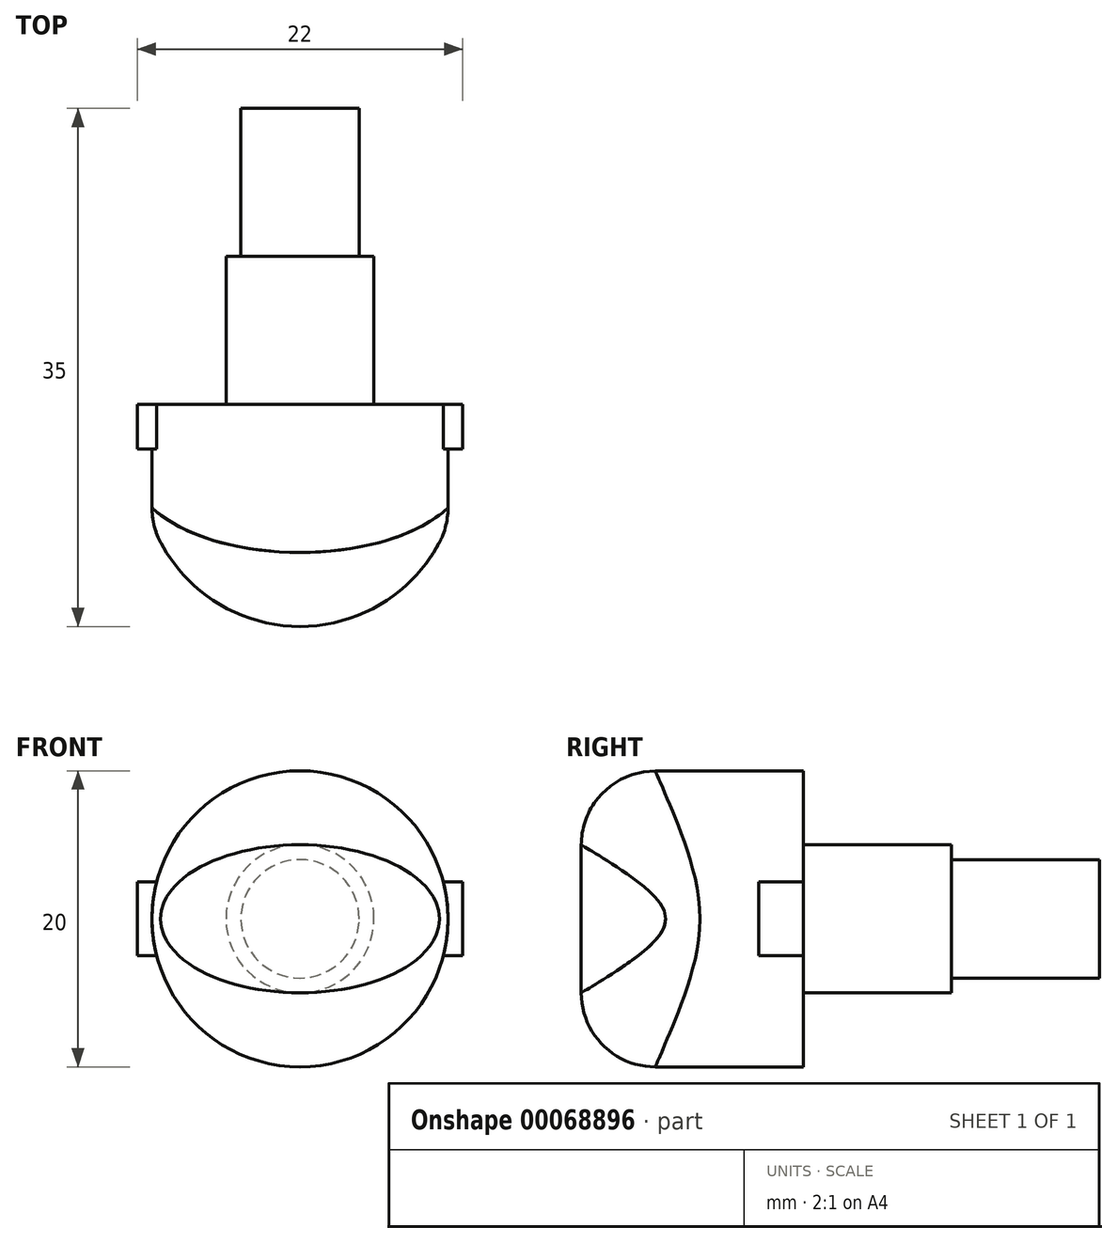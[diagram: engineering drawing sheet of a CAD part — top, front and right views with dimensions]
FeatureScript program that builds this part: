
annotation { "Feature Type Name" : "Feature", "Feature Type Description" : "" }
export const myFeature = defineFeature(function(context is Context, id is Id, definition is map)
    precondition{}
    {
        {
            var Q0;
            Q0=qCreatedBy(makeId("Front.planeOp"),FACE);
            var sketch = newSketch(context, id + "F0", { "sketchPlane" : qUnion([Q0])});
            skCircle(sketch, "E0", {"center": v(0, 0) * mm, "radius": 10 * mm});
            skLineSegment(sketch, "E1", {"start": v(11, 2.5) * mm, "end": v(11, -2.5) * mm});
            skLineSegment(sketch, "E2", {"start": v(11, -2.5) * mm, "end": v(9.68, -2.5) * mm});
            skLineSegment(sketch, "E3", {"start": v(11, 2.5) * mm, "end": v(9.68, 2.5) * mm});
            skLineSegment(sketch, "E4.MirrorCS", {"start": v(-11, -2.5) * mm, "end": v(-9.68, -2.5) * mm});
            skLineSegment(sketch, "E5.MirrorCS", {"start": v(-11, 2.5) * mm, "end": v(-9.68, 2.5) * mm});
            skLineSegment(sketch, "E6.MirrorCS", {"start": v(-11, 2.5) * mm, "end": v(-11, -2.5) * mm});
            skSolve(sketch);
        }
        {
            var Q0;
            Q0=qSketchRegion(id+"F0",true);
            var Q1;
            {var subQ0=sQuery(id+"F0.wireOp",EDGE,"E0");var subQ1=makeQuery(id+"F0.imprint","INTERSECT",VERTEX,{"derivedFrom":[subQ0,sQuery(id+"F0.wireOp",EDGE,"E3")]});Q1=makeQuery(id+"F0.imprint","IMPRINT",FACE,{"disambiguationData":[TD([[makeQuery(id+"F0.imprint","IMPRINT",EDGE,{"disambiguationData":[TD([[subQ1,-1.0]])],"derivedFrom":subQ0}),1.0]])]});}
            extrude(context, id + "F1", {"entities" : qUnion([Q0, Q1]), "oppositeDirection" : true, "depth" : 3 * mm});
        }
        {
            var Q0;
            Q0=qCreatedBy(makeId("Top.planeOp"),FACE);
            var sketch = newSketch(context, id + "F2", { "sketchPlane" : qUnion([Q0])});
            skLineSegment(sketch, "E7", {"start": v(0, 0) * mm, "end": v(-10, 0) * mm});
            skLineSegment(sketch, "E8", {"start": v(-10, 0) * mm, "end": v(-10, -5) * mm});
            skLineSegment(sketch, "E9", {"start": v(0, 0) * mm, "end": v(0, -12) * mm, "construction": true});
            skLineSegment(sketch, "E10", {"start": v(0, 0) * mm, "end": v(10, 0) * mm});
            skLineSegment(sketch, "E11", {"start": v(10, 0) * mm, "end": v(10, -5) * mm});
            skArc(sketch, "E12", {"start": v(-10, -5) * mm, "mid": v(0, -12) * mm, "end": v(10, -5) * mm});
            skSolve(sketch);
        }
        {
            var Q0;
            Q0=makeQuery(id+"F2.imprint","IMPRINT",FACE,{"disambiguationData":[TD([[makeQuery(id+"F2.imprint","IMPRINT",EDGE,{"derivedFrom":sQuery(id+"F2.wireOp",EDGE,"E7")}),1.0]])]});
            extrude(context, id + "F3", {"entities" : qUnion([Q0]), "operationType" : NewBodyOperationType.ADD, "endBound" : BoundingType.SYMMETRIC, "depth" : 20 * mm});
        }
        {
            var Q0;
            Q0=makeQuery(id+"F3.opExtrude","CAP_EDGE",EDGE,{"disambiguationData":[OSD([sQuery(id+"F2.wireOp",EDGE,"E11")])],"isStart":true});
            var Q1;
            Q1=makeQuery(id+"F3.opExtrude","CAP_EDGE",EDGE,{"disambiguationData":[OSD([sQuery(id+"F2.wireOp",EDGE,"E8")])],"isStart":true});
            var Q2;
            Q2=makeQuery(id+"F3.opExtrude","CAP_EDGE",EDGE,{"disambiguationData":[OSD([sQuery(id+"F2.wireOp",EDGE,"E11")])],"isStart":false});
            var Q3;
            Q3=makeQuery(id+"F3.opExtrude","CAP_EDGE",EDGE,{"disambiguationData":[OSD([sQuery(id+"F2.wireOp",EDGE,"E8")])],"isStart":false});
            fillet(context, id + "F4", {"entities" : qUnion([Q0, Q1, Q2, Q3]), "radius" : 10 * mm, "tangentPropagation" : true, "allowEdgeOverflow" : false});
        }
        {
            var Q0;
            Q0=makeQuery(id+"F4.opFillet","BLEND_EDGE",EDGE,{"blendedFrom":[makeQuery(id+"F3.opExtrude","CAP_EDGE",EDGE,{"disambiguationData":[OSD([sQuery(id+"F2.wireOp",EDGE,"E11")])],"isStart":false}),makeQuery(id+"F3.opExtrude","SWEPT_FACE",FACE,{"disambiguationData":[OSD([sQuery(id+"F2.wireOp",EDGE,"E12")])]})],"blendedInto":[makeQuery(id+"F3.opExtrude","SWEPT_FACE",FACE,{"disambiguationData":[OSD([sQuery(id+"F2.wireOp",EDGE,"E12")])]})]});
            var Q1;
            Q1=makeQuery(id+"F4.opFillet","BLEND_EDGE",EDGE,{"blendedFrom":[makeQuery(id+"F3.opExtrude","CAP_EDGE",EDGE,{"disambiguationData":[OSD([sQuery(id+"F2.wireOp",EDGE,"E8")])],"isStart":false}),makeQuery(id+"F3.opExtrude","SWEPT_FACE",FACE,{"disambiguationData":[OSD([sQuery(id+"F2.wireOp",EDGE,"E12")])]})],"blendedInto":[makeQuery(id+"F3.opExtrude","SWEPT_FACE",FACE,{"disambiguationData":[OSD([sQuery(id+"F2.wireOp",EDGE,"E12")])]})]});
            var Q2;
            Q2=makeQuery(id+"F4.opFillet","BLEND_EDGE",EDGE,{"blendedFrom":[makeQuery(id+"F3.opExtrude","CAP_EDGE",EDGE,{"disambiguationData":[OSD([sQuery(id+"F2.wireOp",EDGE,"E11")])],"isStart":true}),makeQuery(id+"F3.opExtrude","SWEPT_FACE",FACE,{"disambiguationData":[OSD([sQuery(id+"F2.wireOp",EDGE,"E12")])]})],"blendedInto":[makeQuery(id+"F3.opExtrude","SWEPT_FACE",FACE,{"disambiguationData":[OSD([sQuery(id+"F2.wireOp",EDGE,"E12")])]})]});
            var Q3;
            Q3=makeQuery(id+"F4.opFillet","BLEND_EDGE",EDGE,{"blendedFrom":[makeQuery(id+"F3.opExtrude","CAP_EDGE",EDGE,{"disambiguationData":[OSD([sQuery(id+"F2.wireOp",EDGE,"E8")])],"isStart":true}),makeQuery(id+"F3.opExtrude","SWEPT_FACE",FACE,{"disambiguationData":[OSD([sQuery(id+"F2.wireOp",EDGE,"E12")])]})],"blendedInto":[makeQuery(id+"F3.opExtrude","SWEPT_FACE",FACE,{"disambiguationData":[OSD([sQuery(id+"F2.wireOp",EDGE,"E12")])]})]});
            fillet(context, id + "F5", {"entities" : qUnion([Q0, Q1, Q2, Q3]), "radius" : 5 * mm, "tangentPropagation" : true, "allowEdgeOverflow" : false});
        }
        {
            var Q0;
            Q0=makeQuery(id+"F1.opExtrude","CAP_FACE",FACE,{"disambiguationData":[OSD([sQuery(id+"F0.wireOp",EDGE,"E0"),sQuery(id+"F0.wireOp",EDGE,"E1"),sQuery(id+"F0.wireOp",EDGE,"E2"),sQuery(id+"F0.wireOp",EDGE,"E3"),sQuery(id+"F0.wireOp",EDGE,"E4.MirrorCS"),sQuery(id+"F0.wireOp",EDGE,"E5.MirrorCS"),sQuery(id+"F0.wireOp",EDGE,"E6.MirrorCS")])],"isStart":false});
            var sketch = newSketch(context, id + "F6", { "sketchPlane" : qUnion([Q0])});
            skCircle(sketch, "E13", {"center": v(0, 0) * mm, "radius": 5 * mm});
            skSolve(sketch);
        }
        {
            var Q0;
            Q0=makeQuery(id+"F6.imprint","IMPRINT",FACE,{"disambiguationData":[TD([[makeQuery(id+"F6.imprint","IMPRINT",EDGE,{"derivedFrom":sQuery(id+"F6.wireOp",EDGE,"E13")}),1.0]])]});
            extrude(context, id + "F7", {"entities" : qUnion([Q0]), "operationType" : NewBodyOperationType.ADD, "depth" : 10 * mm});
        }
        {
            var Q0;
            Q0=makeQuery(id+"F7.opExtrude","CAP_FACE",FACE,{"disambiguationData":[OSD([sQuery(id+"F6.wireOp",EDGE,"E13")])],"isStart":false});
            var sketch = newSketch(context, id + "F8", { "sketchPlane" : qUnion([Q0])});
            skCircle(sketch, "E14", {"center": v(0, 0) * mm, "radius": 4 * mm});
            skSolve(sketch);
        }
        {
            var Q0;
            Q0=qSketchRegion(id+"F8",true);
            var Q1;
            Q1=makeQuery(id+"F8.imprint","IMPRINT",FACE,{"disambiguationData":[TD([[makeQuery(id+"F8.imprint","IMPRINT",EDGE,{"derivedFrom":sQuery(id+"F8.wireOp",EDGE,"E14")}),1.0]])]});
            extrude(context, id + "F9", {"entities" : qUnion([Q0, Q1]), "operationType" : NewBodyOperationType.ADD, "depth" : 10 * mm});
        }
    });
